# Revit family: Kanalhalter SD-LSK
name_source: partatom
category: HLS-Bauteile
revit_build: Autodesk Revit 2017 (Build: 20190507_1515(x64)
units: mm (PartAtom-declared; Revit-internal decimal feet)

## family parameters
Arbeitsebenenbasiert = Ja
Beim Laden mit Abzugskörper schneiden = Nein
Bemaßung runder Anschluss = Durchmesser verwenden
Gemeinsam genutzt = Ja
Immer vertikal = Nein
Raumberechnungspunkt = Nein
Teiletyp = Normal

## types (1)
- Kanalhalter SD-LSK
    Anschluss = M8/M10
    Artikelnummer = 9998376
    Ausführung = schwer
    Bauart = L
    Breite Material = 35 mm
    Dämmelementtyp = genietet
    EAN = 4250928446992
    Fabrikat = MEFA
    Firma = MEFA Befestigungs- und Montagesysteme GmbH
    Gewicht = 0.17 kg
    Gewicht pro Bauteil = 0.17 kg
    Höhe = 80 mm
    Kurztext1 = Kanalhalter LSK (Steigkanal)
    Kurztext2 = Höhe 80 mm Gummi genietet
    Länge = 65 mm  [stored 0.213255 ft]
    Mengeneinheit = St
    Schalldämmeinlage = Gummi SBR
    Stärke Material = 5 mm  [stored 0.0164042 ft]
    Vorgabe-Ansicht = 1219 mm
    max. Temperaturbeständigkeit = 100 °C
    max. zul. Last hängend = 0.80 kN
    max. zul. Last stehend = 0.00 kN
    vpe = 50 St

note: [stored X ft] marks values corroborated as IEEE doubles in the binary element streams (Revit-internal decimal feet)
